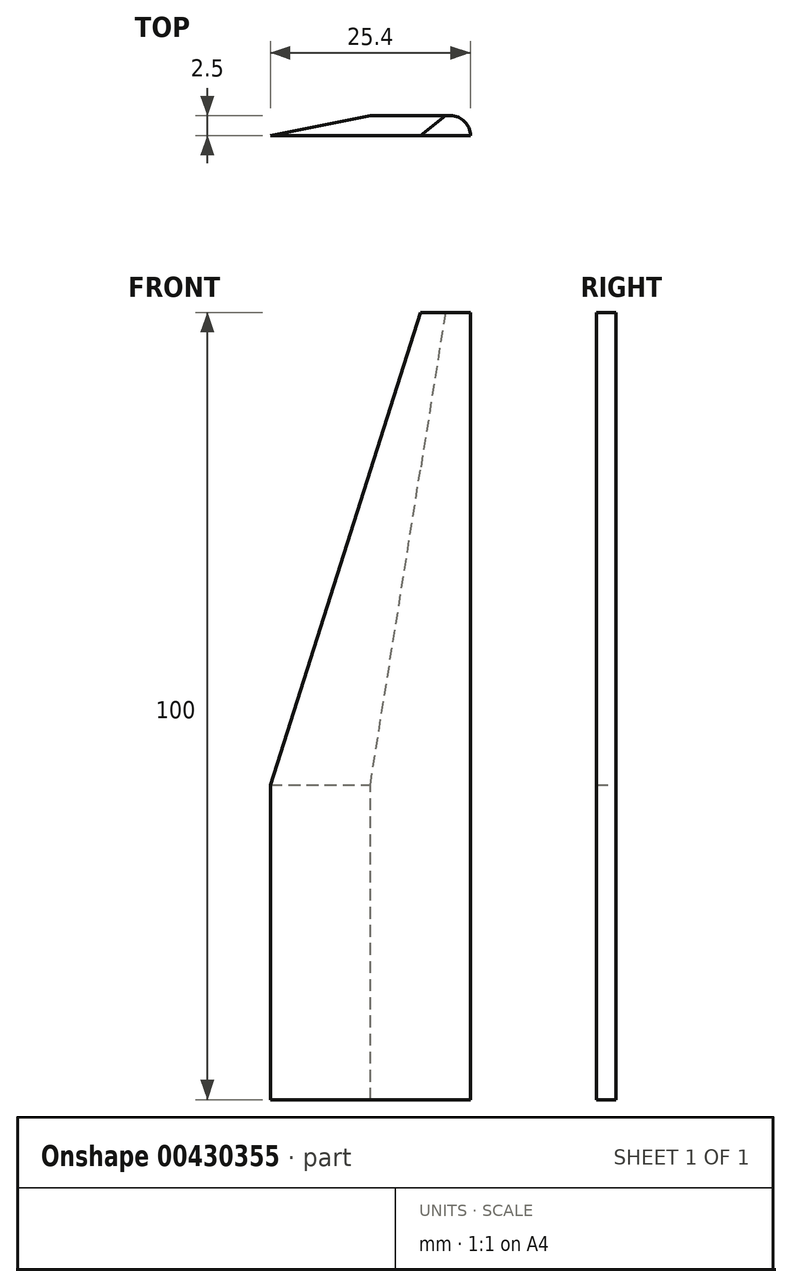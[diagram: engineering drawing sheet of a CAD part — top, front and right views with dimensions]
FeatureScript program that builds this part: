
annotation { "Feature Type Name" : "Feature", "Feature Type Description" : "" }
export const myFeature = defineFeature(function(context is Context, id is Id, definition is map)
    precondition{}
    {
        {
            var Q0;
            Q0=qCreatedBy(makeId("Top.planeOp"),FACE);
            var sketch = newSketch(context, id + "F0", { "sketchPlane" : qUnion([Q0])});
            skLineSegment(sketch, "E0.bottom", {"start": v(12.7, -1.25) * mm, "end": v(-12.7, -1.25) * mm});
            skLineSegment(sketch, "E0.top", {"start": v(12.7, 1.25) * mm, "end": v(0, 1.25) * mm});
            skLineSegment(sketch, "E0.left", {"start": v(12.7, -1.25) * mm, "end": v(12.7, 1.25) * mm});
            skPoint(sketch, "E0.middle", {"position": v(0, 0) * mm});
            skLineSegment(sketch, "E1", {"start": v(-12.7, -1.25) * mm, "end": v(0, 1.25) * mm});
            skPoint(sketch, "E2.orphan", {"position": v(-12.7, 1.25) * mm});
            skSolve(sketch);
        }
        {
            var Q0;
            Q0=qCreatedBy(makeId("Top.planeOp"),FACE);
            cPlane(context, id + "F1", {"entities" : qUnion([Q0]), "cplaneType" : CPlaneType.OFFSET, "offset" : 40 * mm, "width" : 152.4 * mm, "height" : 152.4 * mm});
        }
        {
            var Q0;
            Q0=qCreatedBy(id+"F1.planeOp",FACE);
            var sketch = newSketch(context, id + "F2", { "sketchPlane" : qUnion([Q0])});
            skLineSegment(sketch, "E3.bottom", {"start": v(12.7, -1.25) * mm, "end": v(-12.7, -1.25) * mm});
            skLineSegment(sketch, "E3.top", {"start": v(12.7, 1.25) * mm, "end": v(0, 1.25) * mm});
            skLineSegment(sketch, "E3.left", {"start": v(12.7, -1.25) * mm, "end": v(12.7, 1.25) * mm});
            skPoint(sketch, "E3.middle", {"position": v(0, 0) * mm});
            skLineSegment(sketch, "E4", {"start": v(-12.7, -1.25) * mm, "end": v(0, 1.25) * mm});
            skPoint(sketch, "E3.right.end.orphan", {"position": v(-12.7, 1.25) * mm});
            skSolve(sketch);
        }
        {
            var Q0;
            Q0=qCreatedBy(id+"F1.planeOp",FACE);
            cPlane(context, id + "F3", {"entities" : qUnion([Q0]), "cplaneType" : CPlaneType.OFFSET, "offset" : 40 * mm, "width" : 152.4 * mm, "height" : 152.4 * mm});
        }
        {
            var Q0;
            Q0=qCreatedBy(id+"F3.planeOp",FACE);
            var sketch = newSketch(context, id + "F4", { "sketchPlane" : qUnion([Q0])});
            skLineSegment(sketch, "E5.bottom", {"start": v(12.7, -1.25) * mm, "end": v(0, -1.25) * mm});
            skLineSegment(sketch, "E5.top", {"start": v(12.7, 1.25) * mm, "end": v(6.35, 1.25) * mm});
            skLineSegment(sketch, "E5.left", {"start": v(12.7, -1.25) * mm, "end": v(12.7, 1.25) * mm});
            skPoint(sketch, "E5.middle", {"position": v(0, 0) * mm});
            skLineSegment(sketch, "E6", {"start": v(6.35, 1.25) * mm, "end": v(12.7, 1.25) * mm});
            skLineSegment(sketch, "E7", {"start": v(0, -1.25) * mm, "end": v(6.35, 1.25) * mm});
            skPoint(sketch, "E5.right.start.orphan", {"position": v(-12.7, -1.25) * mm});
            skPoint(sketch, "E8.orphan", {"position": v(-12.7, 1.25) * mm});
            skPoint(sketch, "E9.orphan", {"position": v(0, 1.25) * mm});
            skSolve(sketch);
        }
        {
            var Q0;
            Q0=qSketchRegion(id+"F0",true);
            var Q1;
            Q1=qSketchRegion(id+"F2",true);
            loft(context, id + "F5", {"sheetProfilesArray" : [{ "sheetProfileEntities" : qUnion([Q0]) }, { "sheetProfileEntities" : qUnion([Q1]) }]});
        }
        {
            var Q1;
            Q1=qSketchRegion(id+"F2",true);
            var Q2;
            Q2=qSketchRegion(id+"F4",true);
            loft(context, id + "F6", {"operationType" : NewBodyOperationType.ADD, "sheetProfilesArray" : [{ "sheetProfileEntities" : qUnion([Q1]) }, { "sheetProfileEntities" : qUnion([Q2]) }]});
        }
        {
            var Q0;
            Q0=qCreatedBy(id+"F3.planeOp",FACE);
            cPlane(context, id + "F7", {"entities" : qUnion([Q0]), "cplaneType" : CPlaneType.OFFSET, "offset" : 20 * mm, "width" : 150 * mm, "height" : 150 * mm});
        }
        {
            var Q0;
            Q0=qCreatedBy(id+"F7.planeOp",FACE);
            var sketch = newSketch(context, id + "F8", { "sketchPlane" : qUnion([Q0])});
            skLineSegment(sketch, "E10.bottom", {"start": v(12.7, -1.25) * mm, "end": v(6.35, -1.25) * mm});
            skLineSegment(sketch, "E10.top", {"start": v(12.7, 1.25) * mm, "end": v(9.53, 1.25) * mm});
            skLineSegment(sketch, "E10.left", {"start": v(12.7, -1.25) * mm, "end": v(12.7, 1.25) * mm});
            skPoint(sketch, "E10.middle", {"position": v(0, 0) * mm});
            skLineSegment(sketch, "E11", {"start": v(6.35, -1.25) * mm, "end": v(12.7, -1.25) * mm});
            skLineSegment(sketch, "E12", {"start": v(6.35, -1.25) * mm, "end": v(9.53, 1.25) * mm});
            skPoint(sketch, "E10.right.end.orphan", {"position": v(-12.7, 1.25) * mm});
            skPoint(sketch, "E13.trimOffspring.end.orphan", {"position": v(-12.7, -1.25) * mm});
            skPoint(sketch, "E14.orphan", {"position": v(0, -1.25) * mm});
            skPoint(sketch, "E15.orphan", {"position": v(6.35, 1.25) * mm});
            skLineSegment(sketch, "E16.trimOffspring", {"start": v(9.53, 1.25) * mm, "end": v(12.7, 1.25) * mm});
            skPoint(sketch, "E17.start.orphan", {"position": v(0, 1.25) * mm});
            skSolve(sketch);
        }
        {
            var Q1;
            Q1 = qSketchRegion(id + "F8", true);
            var Q2;
            Q2 = qSketchRegion(id + "F4", true);
            loft(context, id + "F9", {"operationType" : NewBodyOperationType.ADD, "sheetProfilesArray" : [{ "sheetProfileEntities" : qUnion([Q1]) }, { "sheetProfileEntities" : qUnion([Q2]) }]});
        }
        {
            var Q0;
            {var subQ0=sQuery(id+"F4.wireOp",EDGE,"E6");var subQ1=sQuery(id+"F4.wireOp",EDGE,"E5.left");var subQ2=sQuery(id+"F2.wireOp",EDGE,"E3.left");var subQ3=sQuery(id+"F2.wireOp",EDGE,"E3.top");Q0=makeQuery(id+"F9.boolean.opBoolean","MERGE",EDGE,{"derivedFrom":[makeQuery(id+"F6.boolean.opBoolean","MERGE",EDGE,{"derivedFrom":[makeQuery(id+"F5.opLoft","SWEPT_EDGE",EDGE,{"disambiguationData":[OSD([sQuery(id+"F0.wireOp",EDGE,"E0.top"),sQuery(id+"F0.wireOp",EDGE,"E0.left"),subQ3,subQ2])]}),makeQuery(id+"F6.opLoft","SWEPT_EDGE",EDGE,{"disambiguationData":[OSD([subQ3,subQ2,subQ1,subQ0])]})]}),makeQuery(id+"F9.opLoft","SWEPT_EDGE",EDGE,{"disambiguationData":[OSD([subQ1,subQ0,sQuery(id+"F8.wireOp",EDGE,"E10.left"),sQuery(id+"F8.wireOp",EDGE,"E16.trimOffspring")])]})]});}
            fillet(context, id + "F10", {"entities" : qUnion([Q0]), "radius" : 2.5 * mm, "tangentPropagation" : true, "allowEdgeOverflow" : false});
        }
    });
